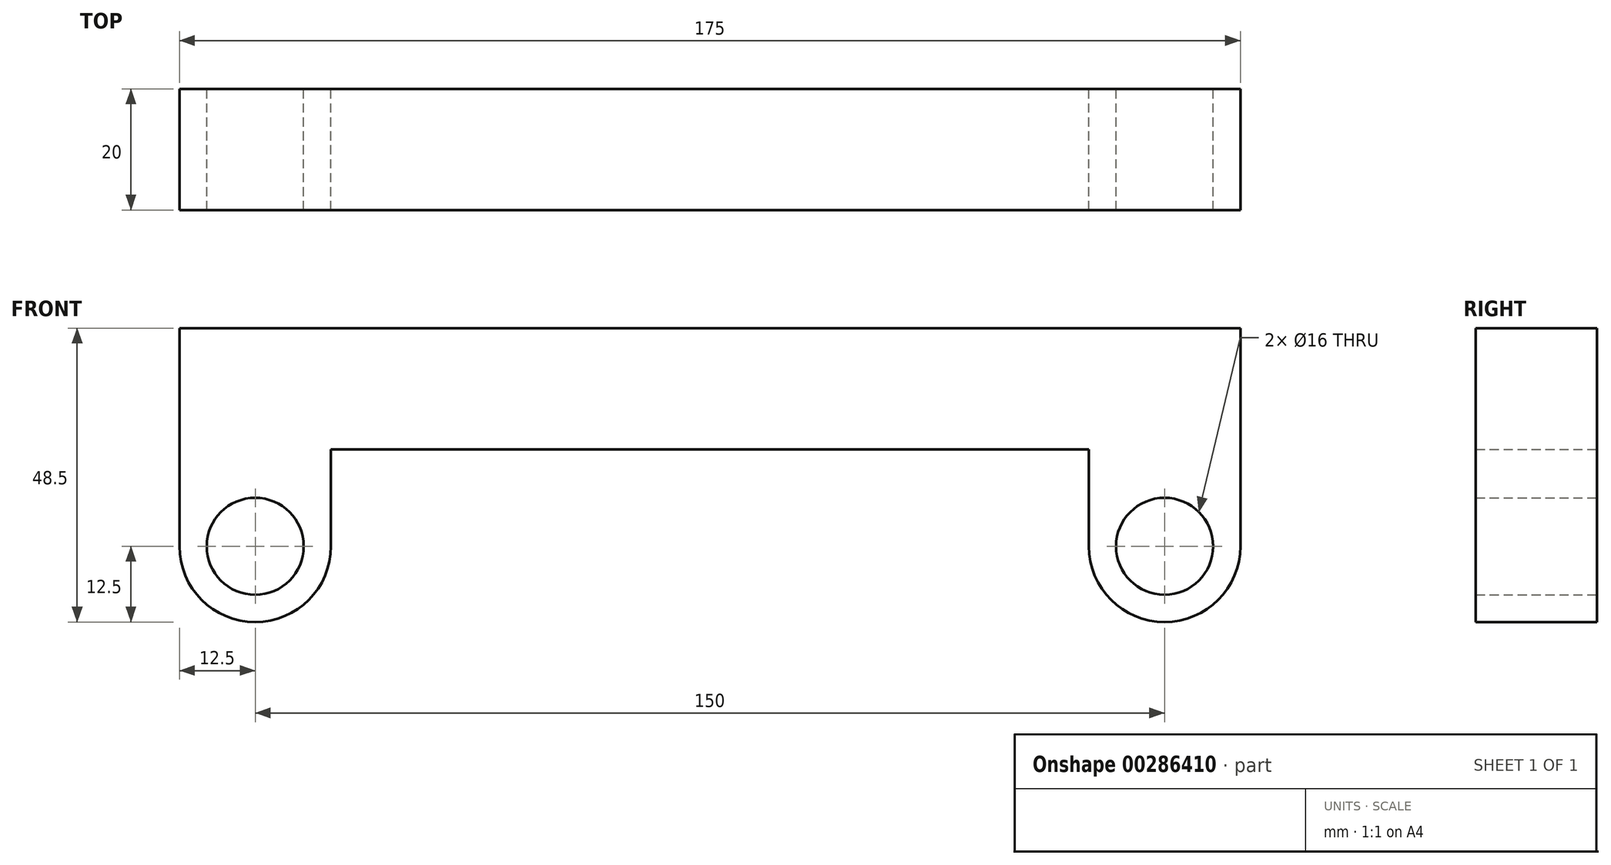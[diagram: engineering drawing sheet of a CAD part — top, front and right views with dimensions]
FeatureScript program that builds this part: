
annotation { "Feature Type Name" : "Feature", "Feature Type Description" : "" }
export const myFeature = defineFeature(function(context is Context, id is Id, definition is map)
    precondition{}
    {
        {
            var Q0;
            Q0=qCreatedBy(makeId("Front.planeOp"),FACE);
            var sketch = newSketch(context, id + "F0", { "sketchPlane" : qUnion([Q0])});
            skLineSegment(sketch, "E0", {"start": v(-125, 36) * mm, "end": v(50, 36) * mm});
            skLineSegment(sketch, "E1", {"start": v(50, 36) * mm, "end": v(50, 0) * mm});
            skLineSegment(sketch, "E2", {"start": v(25, 0) * mm, "end": v(25, 16) * mm});
            skLineSegment(sketch, "E3", {"start": v(25, 16) * mm, "end": v(-100, 16) * mm});
            skLineSegment(sketch, "E4", {"start": v(-100, 16) * mm, "end": v(-100, 0) * mm});
            skLineSegment(sketch, "E5", {"start": v(-125, 0) * mm, "end": v(-125, 36) * mm});
            skArc(sketch, "E6", {"start": v(-125, 0) * mm, "mid": v(-112.5, -12.5) * mm, "end": v(-100, 0) * mm});
            skArc(sketch, "E7", {"start": v(25, 0) * mm, "mid": v(37.5, -12.5) * mm, "end": v(50, 0) * mm});
            skPoint(sketch, "E8.orphan", {"position": v(25, -12.5) * mm});
            skPoint(sketch, "E9.orphan", {"position": v(-100, -12.5) * mm});
            skSolve(sketch);
        }
        {
            var Q0;
            Q0 = qSketchRegion(id + "F0", true);
            extrude(context, id + "F1", {"entities" : qUnion([Q0]), "depth" : 10 * mm, "hasSecondDirection" : true, "secondDirectionOppositeDirection" : true, "secondDirectionDepth" : 10 * mm});
        }
        {
            var Q0;
            Q0=qCreatedBy(makeId("Front.planeOp"),FACE);
            var sketch = newSketch(context, id + "F2", { "sketchPlane" : qUnion([Q0])});
            skCircle(sketch, "E10", {"center": v(-112.5, 0) * mm, "radius": 8 * mm});
            skCircle(sketch, "E11", {"center": v(37.5, 0) * mm, "radius": 8 * mm});
            skSolve(sketch);
        }
        {
            var Q0;
            Q0 = qSketchRegion(id + "F2", true);
            extrude(context, id + "F3", {"entities" : qUnion([Q0]), "operationType" : NewBodyOperationType.REMOVE, "endBound" : BoundingType.UP_TO_NEXT, "depth" : 25 * mm, "hasSecondDirection" : true, "secondDirectionBound" : SecondDirectionBoundingType.UP_TO_NEXT, "secondDirectionOppositeDirection" : true, "secondDirectionDepth" : 25 * mm});
        }
    });
